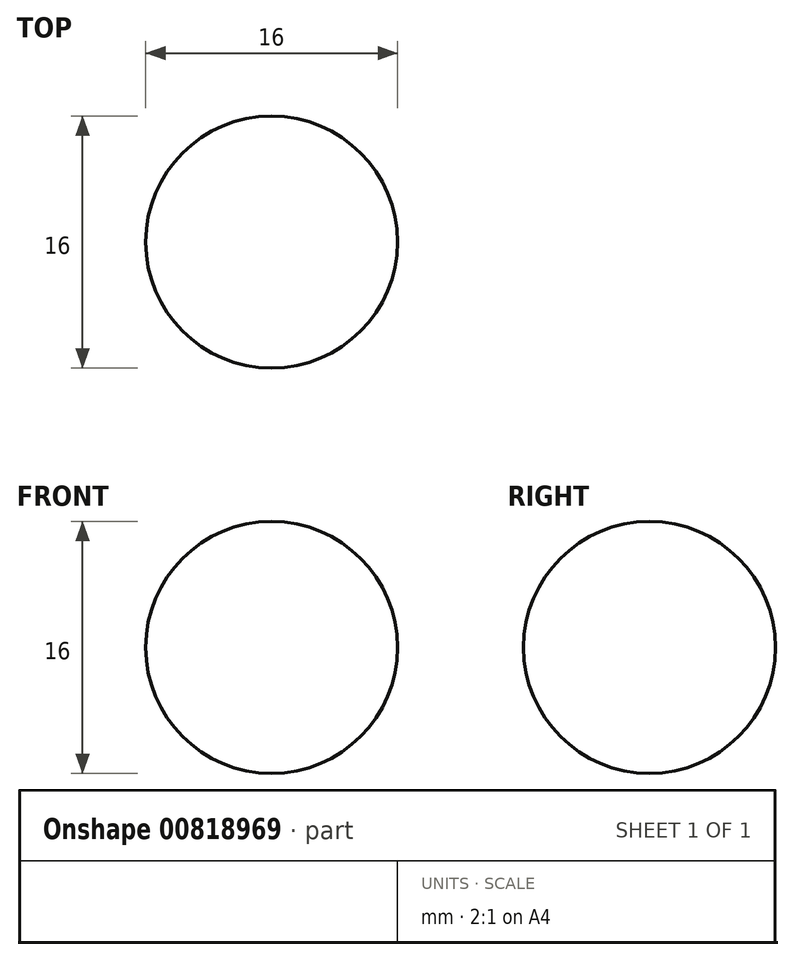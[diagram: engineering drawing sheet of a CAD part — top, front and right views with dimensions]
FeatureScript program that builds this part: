
annotation { "Feature Type Name" : "Feature", "Feature Type Description" : "" }
export const myFeature = defineFeature(function(context is Context, id is Id, definition is map)
    precondition{}
    {
        {
            var Q0;
            Q0=qCreatedBy(makeId("Right.planeOp"),FACE);
            var sketch = newSketch(context, id + "F0", { "sketchPlane" : qUnion([Q0])});
            skArc(sketch, "E0", {"start": v(0, 8) * mm, "mid": v(-8, 0) * mm, "end": v(0, -8) * mm});
            skLineSegment(sketch, "E1", {"start": v(0, -21.26) * mm, "end": v(0, 30.92) * mm, "construction": true});
            skLineSegment(sketch, "E2", {"start": v(0, 8) * mm, "end": v(0, -8) * mm});
            skSolve(sketch);
        }
        {
            var Q0;
            Q0=makeQuery(id+"F0.imprint","IMPRINT",FACE,{"disambiguationData":[TD([[makeQuery(id+"F0.imprint","IMPRINT",EDGE,{"derivedFrom":sQuery(id+"F0.wireOp",EDGE,"E0")}),1.0]])]});
            var Q1;
            Q1=sQuery(id+"F0.wireOp",EDGE,"E1");
            revolve(context, id + "F1", {"surfaceOperationType" : NewSurfaceOperationType.NEW, "entities" : qUnion([Q0]), "axis" : qUnion([Q1]), "revolveType" : RevolveType.FULL});
        }
    });
